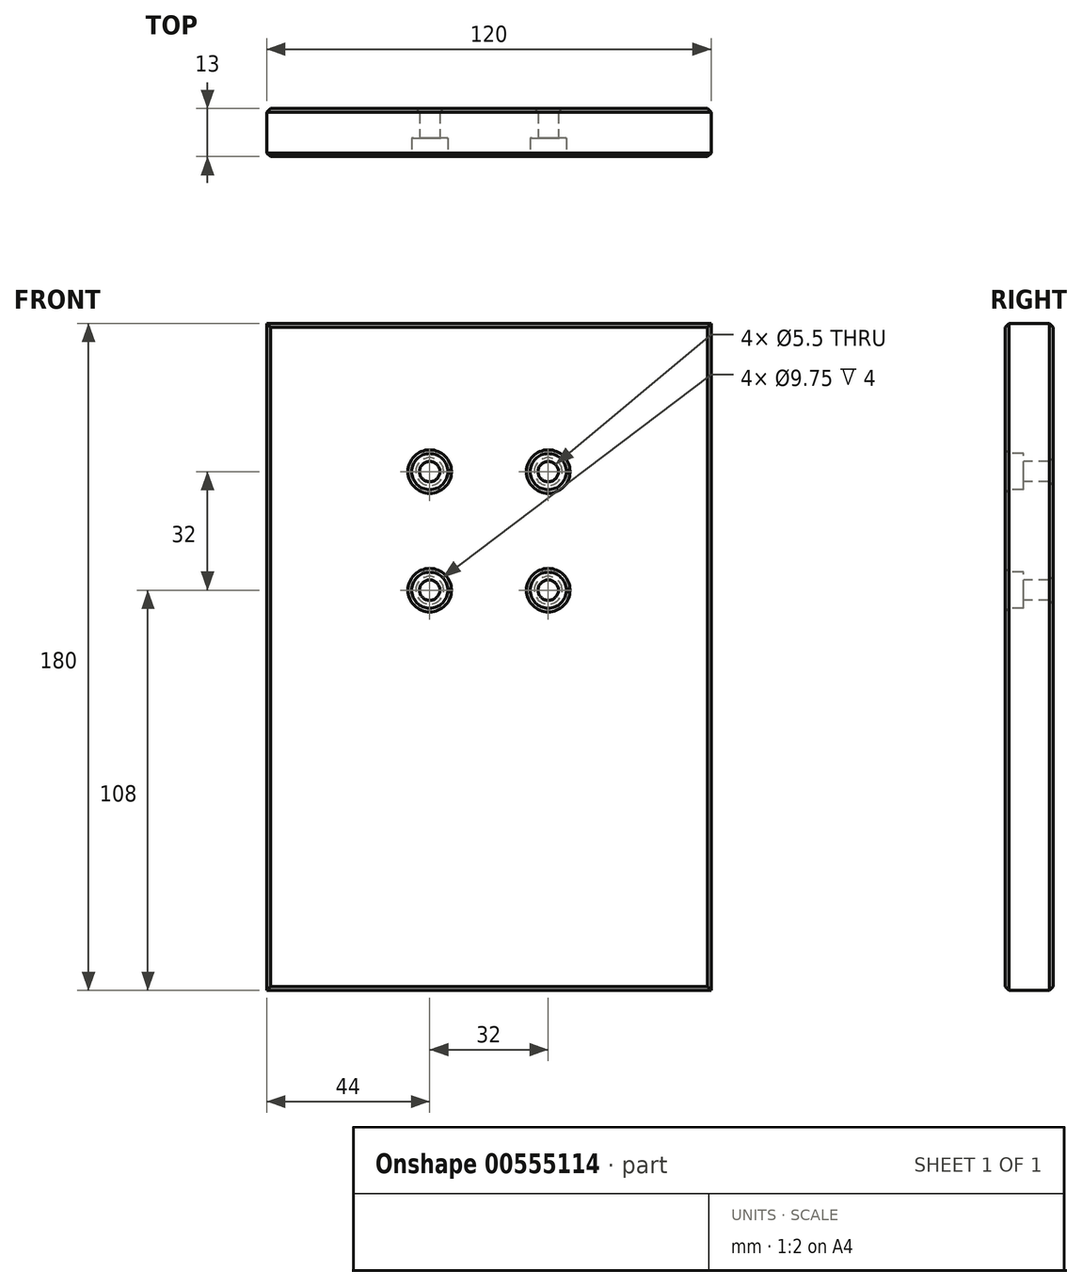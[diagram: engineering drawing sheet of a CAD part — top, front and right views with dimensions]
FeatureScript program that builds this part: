
annotation { "Feature Type Name" : "Feature", "Feature Type Description" : "" }
export const myFeature = defineFeature(function(context is Context, id is Id, definition is map)
    precondition{}
    {
        {
            var Q0;
            Q0=qCreatedBy(makeId("Front.planeOp"),FACE);
            var sketch = newSketch(context, id + "F0", { "sketchPlane" : qUnion([Q0])});
            skLineSegment(sketch, "E0.bottom", {"start": v(0, 0) * mm, "end": v(120, 0) * mm});
            skLineSegment(sketch, "E0.top", {"start": v(0, 180) * mm, "end": v(120, 180) * mm});
            skLineSegment(sketch, "E0.left", {"start": v(0, 0) * mm, "end": v(0, 180) * mm});
            skLineSegment(sketch, "E0.right", {"start": v(120, 0) * mm, "end": v(120, 180) * mm});
            skSolve(sketch);
        }
        {
            var Q0;
            Q0 = qSketchRegion(id + "F0", true);
            var Q1;
            Q1=makeQuery(id+"F0.imprint","IMPRINT",FACE,{"disambiguationData":[TD([[makeQuery(id+"F0.imprint","IMPRINT",EDGE,{"derivedFrom":sQuery(id+"F0.wireOp",EDGE,"E0.bottom")}),1.0]])]});
            extrude(context, id + "F1", {"entities" : qUnion([Q0, Q1]), "depth" : 13 * mm, "offsetDistance" : 25 * mm});
        }
        {
            var Q0;
            Q0=makeQuery(id+"F1.opExtrude","CAP_FACE",FACE,{"disambiguationData":[OSD([sQuery(id+"F0.wireOp",EDGE,"E0.bottom"),sQuery(id+"F0.wireOp",EDGE,"E0.top"),sQuery(id+"F0.wireOp",EDGE,"E0.left"),sQuery(id+"F0.wireOp",EDGE,"E0.right")])],"isStart":false});
            var sketch = newSketch(context, id + "F2", { "sketchPlane" : qUnion([Q0])});
            skPoint(sketch, "E1", {"position": v(44, 140) * mm});
            skPoint(sketch, "E2", {"position": v(76, 140) * mm});
            skPoint(sketch, "E3", {"position": v(76, 108) * mm});
            skPoint(sketch, "E4", {"position": v(44, 108) * mm});
            skSolve(sketch);
        }
        {
            var Q0;
            Q0=sQuery(id+"F2.wireOp",VERTEX,"E1");
            var Q1;
            Q1=sQuery(id+"F2.wireOp",VERTEX,"E4");
            var Q2;
            Q2=sQuery(id+"F2.wireOp",VERTEX,"E2");
            var Q3;
            Q3=sQuery(id+"F2.wireOp",VERTEX,"E3");
            var Q4;
            Q4=makeQuery(id+"F1.opExtrude","SWEPT_BODY",BODY,{"disambiguationData":[OSD([sQuery(id+"F0.wireOp",EDGE,"E0.bottom"),sQuery(id+"F0.wireOp",EDGE,"E0.top"),sQuery(id+"F0.wireOp",EDGE,"E0.left"),sQuery(id+"F0.wireOp",EDGE,"E0.right")])]});
            hole(context, id + "F3", {"style" : HoleStyle.C_BORE, "endStyle" : HoleEndStyle.THROUGH, "standardTappedOrClearance" : lookupTablePath({ "standard" : "ISO", "fit" : "Normal", "size" : "M5", "type" : "Clearance" }), "standardBlindInLast" : lookupTablePath({ "fit" : "Standard", "standard" : "ISO", "size" : "M5", "type" : "Clearance" }), "holeDiameter" : 5.5 * mm, "cBoreDiameter" : 9.75 * mm, "cBoreDepth" : 5 * mm, "isTappedThrough" : true, "tappedDepth" : 8 * mm, "tapClearance" : 3, "startFromSketch" : true, "locations" : qUnion([Q0, Q1, Q2, Q3]), "scope" : qUnion([Q4])});
        }
        {
            var Q0;
            Q0=makeQuery(id+"F1.opExtrude","CAP_EDGE",EDGE,{"disambiguationData":[OSD([sQuery(id+"F0.wireOp",EDGE,"E0.top")])],"isStart":false});
            var Q1;
            Q1=makeQuery(id+"F1.opExtrude","CAP_EDGE",EDGE,{"disambiguationData":[OSD([sQuery(id+"F0.wireOp",EDGE,"E0.left")])],"isStart":false});
            var Q2;
            Q2=makeQuery(id+"F1.opExtrude","CAP_FACE",FACE,{"disambiguationData":[OSD([sQuery(id+"F0.wireOp",EDGE,"E0.bottom"),sQuery(id+"F0.wireOp",EDGE,"E0.top"),sQuery(id+"F0.wireOp",EDGE,"E0.left"),sQuery(id+"F0.wireOp",EDGE,"E0.right")])],"isStart":false});
            chamfer(context, id + "F4", {"entities" : qUnion([Q0, Q1, Q2]), "width" : 1 * mm, "tangentPropagation" : true});
        }
        {
            var Q0;
            Q0=makeQuery(id+"F1.opExtrude","CAP_FACE",FACE,{"disambiguationData":[OSD([sQuery(id+"F0.wireOp",EDGE,"E0.bottom"),sQuery(id+"F0.wireOp",EDGE,"E0.top"),sQuery(id+"F0.wireOp",EDGE,"E0.left"),sQuery(id+"F0.wireOp",EDGE,"E0.right")])],"isStart":true});
            chamfer(context, id + "F5", {"entities" : qUnion([Q0]), "width" : 1 * mm, "tangentPropagation" : true});
        }
    });
